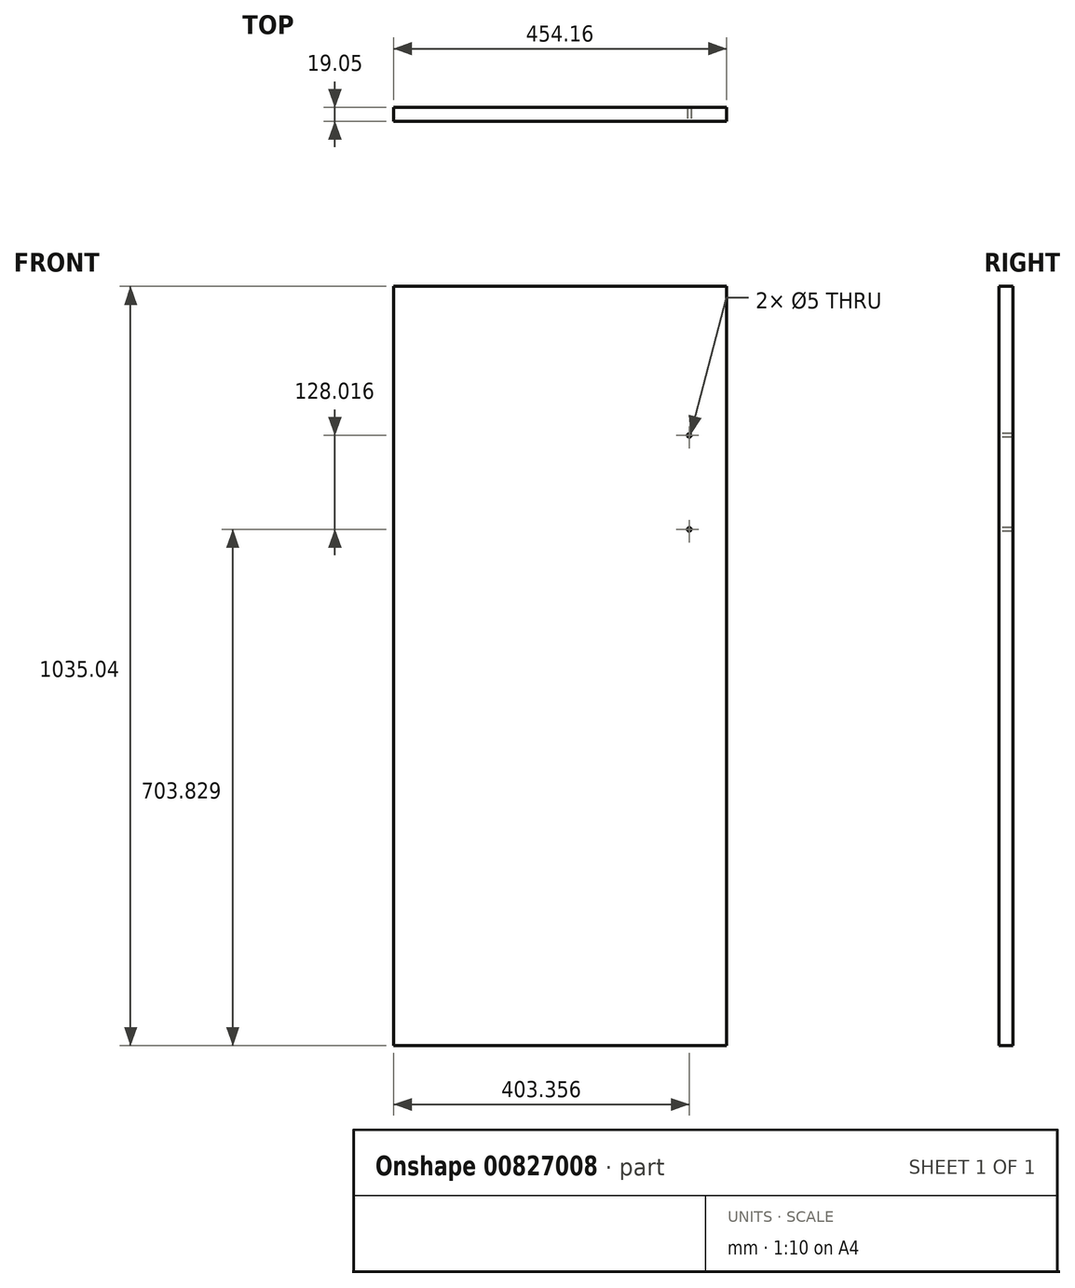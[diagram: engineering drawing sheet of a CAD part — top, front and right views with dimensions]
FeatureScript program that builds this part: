
annotation { "Feature Type Name" : "Feature", "Feature Type Description" : "" }
export const myFeature = defineFeature(function(context is Context, id is Id, definition is map)
    precondition{}
    {
        {
            var Q0;
            Q0=qCreatedBy(makeId("Front.planeOp"),FACE);
            var sketch = newSketch(context, id + "F0", { "sketchPlane" : qUnion([Q0])});
            skLineSegment(sketch, "E0.bottom", {"start": v(227.08, 517.52) * mm, "end": v(-227.08, 517.52) * mm});
            skLineSegment(sketch, "E0.top", {"start": v(227.08, -517.53) * mm, "end": v(-227.08, -517.53) * mm});
            skLineSegment(sketch, "E0.left", {"start": v(227.08, 517.52) * mm, "end": v(227.08, -517.53) * mm});
            skLineSegment(sketch, "E0.right", {"start": v(-227.08, 517.52) * mm, "end": v(-227.08, -517.53) * mm});
            skPoint(sketch, "E0.middle", {"position": v(0, 0) * mm});
            skSolve(sketch);
        }
        {
            var Q0;
            Q0=makeQuery(id+"F0.imprint","IMPRINT",FACE,{"disambiguationData":[TD([[makeQuery(id+"F0.imprint","IMPRINT",EDGE,{"derivedFrom":sQuery(id+"F0.wireOp",EDGE,"E0.bottom")}),1.0]])]});
            extrude(context, id + "F1", {"entities" : qUnion([Q0]), "depth" : 19.05 * mm, "offsetDistance" : 25.4 * mm});
        }
        {
            var Q0;
            Q0=makeQuery(id+"F1.opExtrude","CAP_FACE",FACE,{"disambiguationData":[OSD([sQuery(id+"F0.wireOp",EDGE,"E0.bottom"),sQuery(id+"F0.wireOp",EDGE,"E0.top"),sQuery(id+"F0.wireOp",EDGE,"E0.left"),sQuery(id+"F0.wireOp",EDGE,"E0.right")])],"isStart":false});
            var sketch = newSketch(context, id + "F2", { "sketchPlane" : qUnion([Q0])});
            skLineSegment(sketch, "E1", {"start": v(227.08, 517.52) * mm, "end": v(176.28, 517.52) * mm});
            skLineSegment(sketch, "E2", {"start": v(176.28, 517.52) * mm, "end": v(176.28, 314.32) * mm});
            skLineSegment(sketch, "E3", {"start": v(176.28, 314.32) * mm, "end": v(176.28, 186.3) * mm});
            skSolve(sketch);
        }
        {
            var Q0;
            Q0=sQuery(id+"F2.wireOp",VERTEX,"E2.end");
            var Q1;
            Q1=sQuery(id+"F2.wireOp",VERTEX,"E3.end");
            var Q2;
            Q2=makeQuery(id+"F1.opExtrude","SWEPT_BODY",BODY,{"disambiguationData":[OSD([sQuery(id+"F0.wireOp",EDGE,"E0.bottom"),sQuery(id+"F0.wireOp",EDGE,"E0.top"),sQuery(id+"F0.wireOp",EDGE,"E0.left"),sQuery(id+"F0.wireOp",EDGE,"E0.right")])]});
            hole(context, id + "F3", {"style" : HoleStyle.SIMPLE, "endStyle" : HoleEndStyle.BLIND, "holeDiameter" : 5 * mm, "majorDiameter" : 6.35 * mm, "holeDepth" : 25.4 * mm, "isTappedThrough" : true, "tappedDepth" : 12.7 * mm, "tapClearance" : 3, "startFromSketch" : true, "locations" : qUnion([Q0, Q1]), "scope" : qUnion([Q2])});
        }
    });
